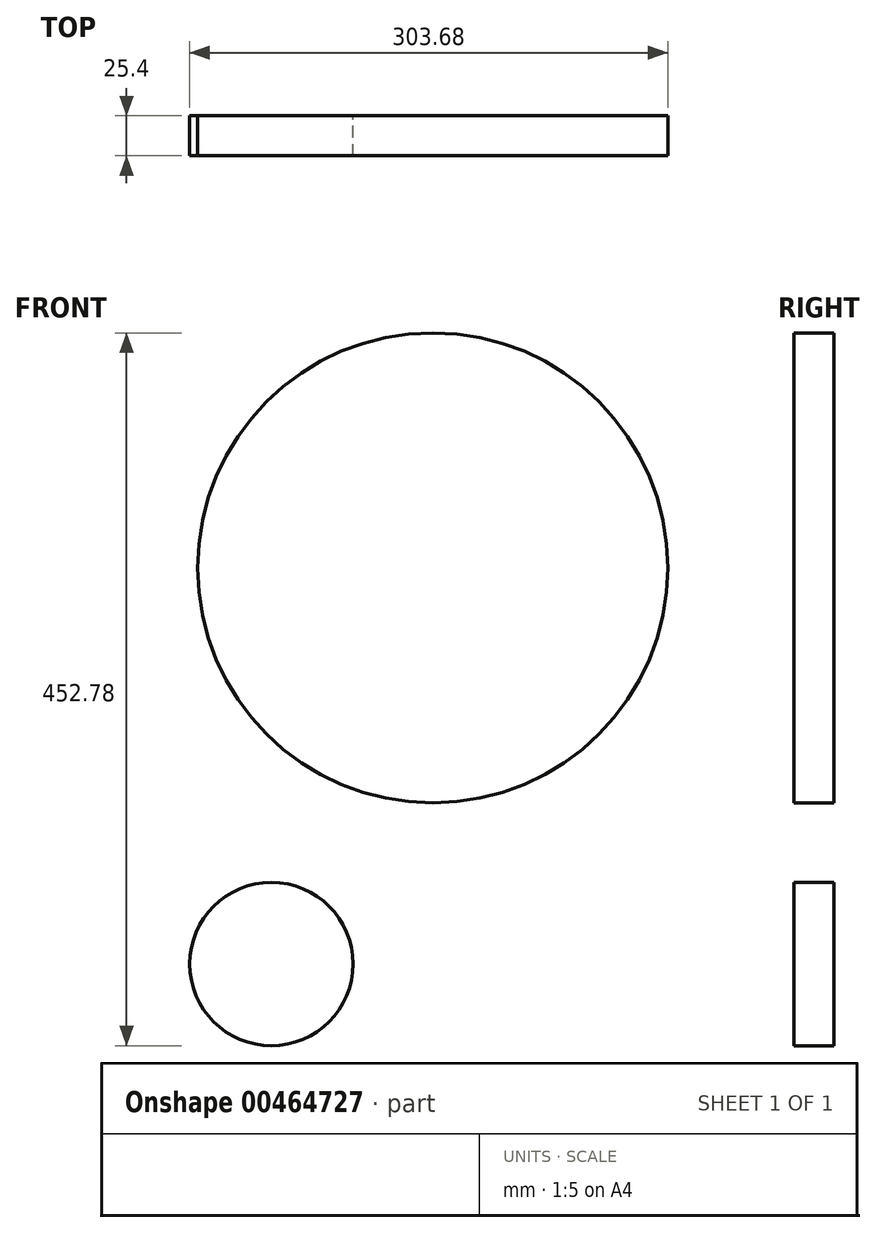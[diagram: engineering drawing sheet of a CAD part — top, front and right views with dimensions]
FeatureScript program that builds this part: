
annotation { "Feature Type Name" : "Feature", "Feature Type Description" : "" }
export const myFeature = defineFeature(function(context is Context, id is Id, definition is map)
    precondition{}
    {
        {
            var Q0;
            Q0=qCreatedBy(makeId("Front.planeOp"),FACE);
            var sketch = newSketch(context, id + "F0", { "sketchPlane" : qUnion([Q0])});
            skCircle(sketch, "E0", {"center": v(0, 0) * mm, "radius": 51.88 * mm});
            skCircle(sketch, "E1", {"center": v(102.51, 251.62) * mm, "radius": 149.28 * mm});
            skCircle(sketch, "E2", {"center": v(21.5, 0) * mm, "radius": 30.38 * mm});
            skSolve(sketch);
        }
        {
            var Q0;
            Q0 = qSketchRegion(id + "F0", true);
            extrude(context, id + "F1", {"entities" : qUnion([Q0]), "depth" : 25.4 * mm});
        }
    });
